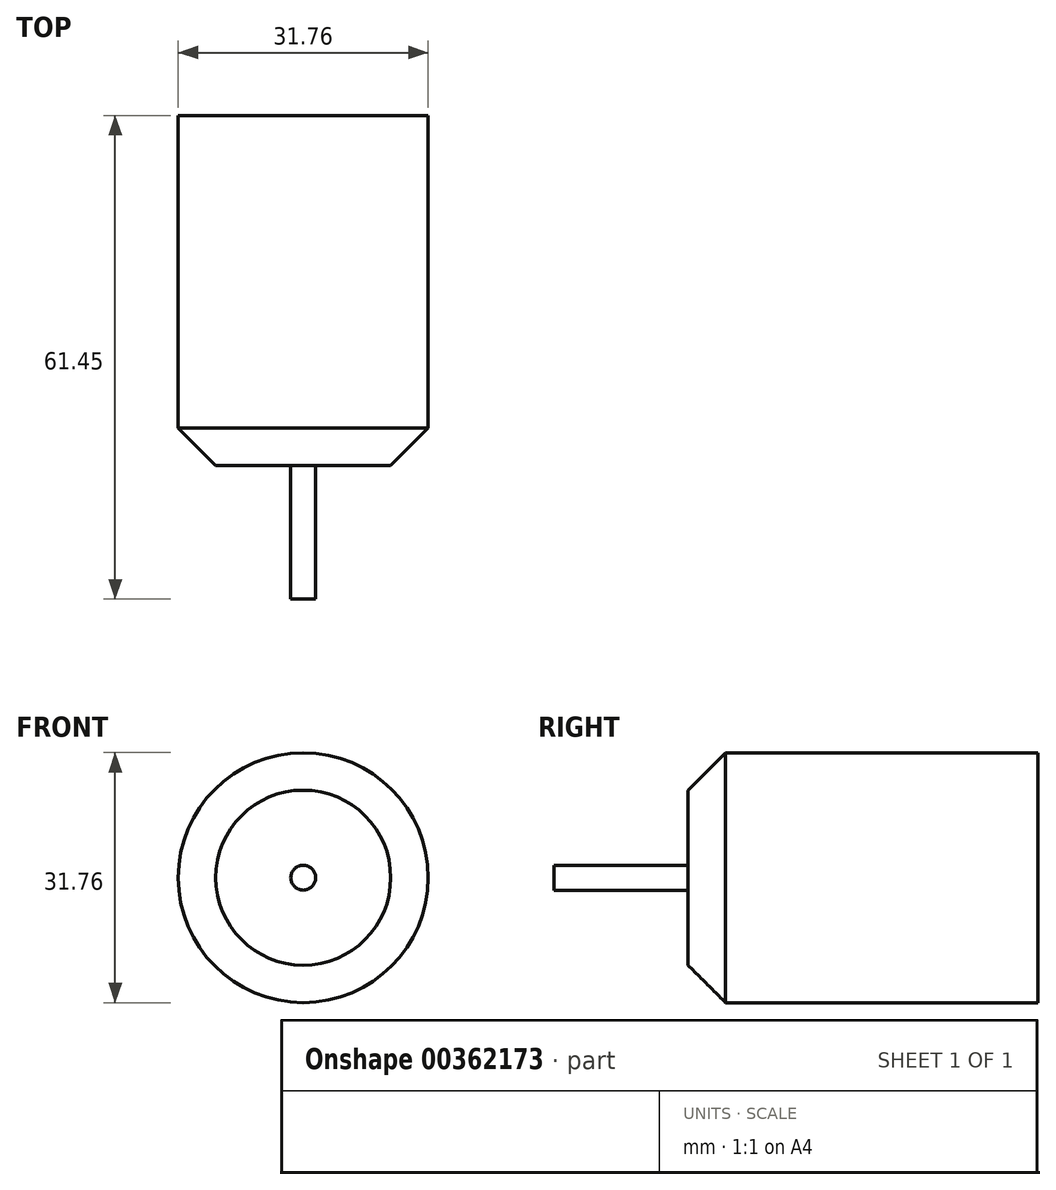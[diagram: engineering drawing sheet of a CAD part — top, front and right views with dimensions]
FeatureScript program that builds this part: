
annotation { "Feature Type Name" : "Feature", "Feature Type Description" : "" }
export const myFeature = defineFeature(function(context is Context, id is Id, definition is map)
    precondition{}
    {
        {
            var Q0;
            Q0=qCreatedBy(makeId("Front.planeOp"),FACE);
            var sketch = newSketch(context, id + "F0", { "sketchPlane" : qUnion([Q0])});
            skCircle(sketch, "E0", {"center": v(0, 0) * mm, "radius": 15.87 * mm});
            skSolve(sketch);
        }
        {
            var Q0;
            Q0=makeQuery(id+"F0.imprint","IMPRINT",FACE,{"disambiguationData":[TD([[makeQuery(id+"F0.imprint","IMPRINT",EDGE,{"derivedFrom":sQuery(id+"F0.wireOp",EDGE,"E0")}),1.0]])]});
            extrude(context, id + "F1", {"entities" : qUnion([Q0]), "depth" : 44.45 * mm});
        }
        {
            var Q0;
            Q0=makeQuery(id+"F1.opExtrude","CAP_EDGE",EDGE,{"disambiguationData":[OSD([sQuery(id+"F0.wireOp",EDGE,"E0")])],"isStart":false});
            chamfer(context, id + "F2", {"entities" : qUnion([Q0]), "width" : 4.76 * mm, "tangentPropagation" : true});
        }
        {
            var Q0;
            Q0=makeQuery(id+"F1.opExtrude","CAP_FACE",FACE,{"disambiguationData":[OSD([sQuery(id+"F0.wireOp",EDGE,"E0")])],"isStart":false});
            var sketch = newSketch(context, id + "F3", { "sketchPlane" : qUnion([Q0])});
            skCircle(sketch, "E1", {"center": v(0, 0) * mm, "radius": 1.59 * mm});
            skSolve(sketch);
        }
        {
            var Q0;
            Q0=makeQuery(id+"F3.imprint","IMPRINT",FACE,{"disambiguationData":[TD([[makeQuery(id+"F3.imprint","IMPRINT",EDGE,{"derivedFrom":sQuery(id+"F3.wireOp",EDGE,"E1")}),1.0]])]});
            extrude(context, id + "F4", {"entities" : qUnion([Q0]), "operationType" : NewBodyOperationType.ADD, "depth" : 17 * mm});
        }
    });
